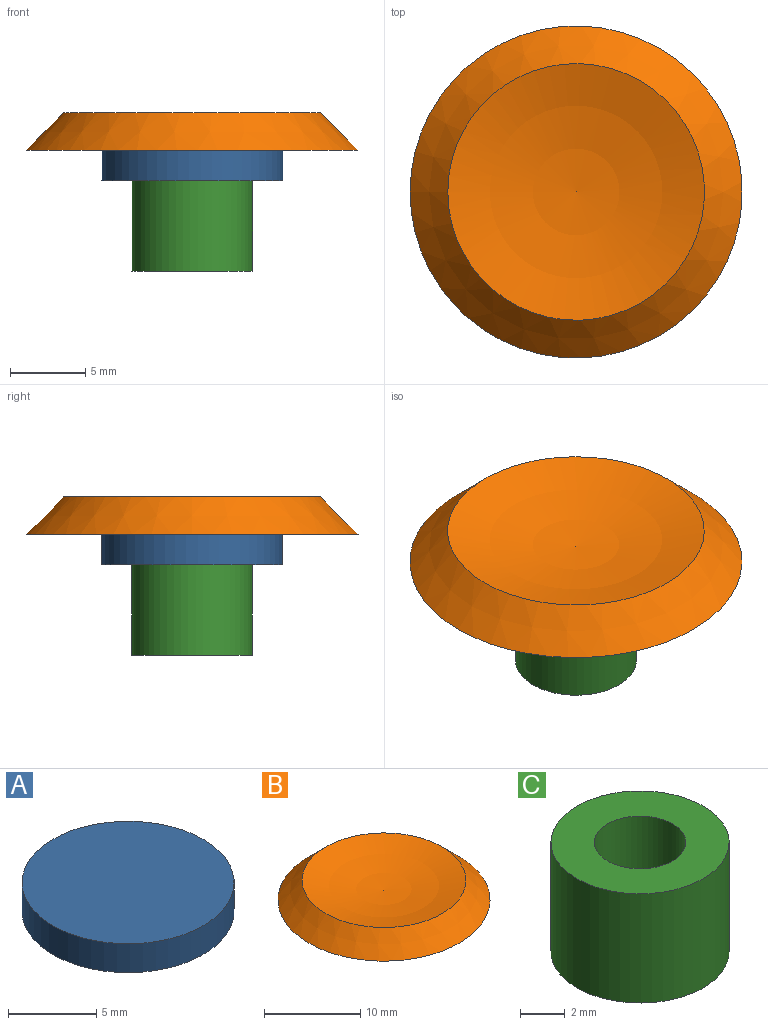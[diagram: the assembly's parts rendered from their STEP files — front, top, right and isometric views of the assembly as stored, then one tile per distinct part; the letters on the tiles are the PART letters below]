
ASSEMBLY  parts=3 mates=2
PART A: 3 faces, bbox 12x12x2 mm
  f0: cylinder r=6mm len=12mm, axis (0,0,-1), area 75.4mm2, adj f1,f2
  f1: plane 12x12mm, normal (0,0,1), area 113.1mm2, adj f0
  f2: plane 12x12mm, normal (0,0,-1), area 113.1mm2, adj f0
PART B: 3 faces, bbox 22x22x2.5 mm
  f0: plane 22x22mm, normal (0,0,-1), area 380.1mm2, adj f1
  f1: cone r=11mm half-angle=45deg, axis (0,0,-1), area 216.6mm2, adj f0,f2
  f2: sphere r=29.52mm, area 231.9mm2, adj f1
PART C: 4 faces, bbox 8x8x6 mm
  f0: cylinder r=2.05mm len=6mm, axis (0,0,-1), area 77.3mm2, adj f2,f3
  f1: cylinder r=4mm len=8mm, axis (0,0,-1), area 150.8mm2, adj f2,f3
  f2: plane 8x8mm, normal (0,0,1), area 37.1mm2, adj f0,f1
  f3: plane 8x8mm, normal (0,0,-1), area 37.1mm2, adj f0,f1
PLACE A t=(57.29,-15.54,26.91)mm
PLACE B t=(5.81,23.13,28.91)mm
PLACE C t=(37.85,-0.18,20.91)mm
MATE fastened C.f0 <-> A.f0  axis (0,0,1) through (5.81,23.13,26.91)mm
MATE fastened A.f0 <-> B.f1  axis (0,0,1) through (5.81,23.13,28.91)mm
